# Revit family: BOLA DISC FLUSH
name_source: partatom
category: Lighting Fixtures
revit_build: Autodesk Revit 2017 (Build: 20160225_1515(x64)
units: mm (PartAtom-declared; Revit-internal decimal feet)

## family parameters
Always vertical = Yes
Cut with Voids When Loaded = No
Light Source = Yes
OmniClass Number = 23.80.70.00
OmniClass Title = Lighting
Part Type = Normal
Room Calculation Point = No
Round Connector Dimension = Use Diameter
Shared = No
Work Plane-Based = No

## types (4) — shared parameters
Color Filter = 16777215
Color Rendition Index = 95 CRI
Color Temperature = 2700K - 1800K (Warm Dim)
Dimming Lamp Color Temperature Shift = <None>
Emit Shape Visible in Rendering = No
Emit from Circle Diameter = 2' - 0"
Lifespan = 50K hour lifespan
Luminaire Efficacy = 65 Lumens/Watt (average)
Luminosity = 290Lm
Note = 3000K CCT models and 2700 CCT models
Power Consumption = 6W
Tilt Angle = 90.00°
Voltage = 120-277V 50/60Hz

## per-type parameters (varying)
| type | Photometric Web File |
| BOLA DISC FLUSH - 12 | bola4_IESNA2002_2018.ies |
| BOLA DISC FLUSH - 18 | bola5_IESNA2002_2018.ies |
| BOLA DISC FLUSH - 22 | bola6_IESNA2002_2018.ies |
| BOLA DISC FLUSH - 32 | bola8_IESNA2002_2018.ies |

type visibility flags: 4 boolean params named "<type name>" — each type sets only its own to Yes (folded from table)

## geometry (parser evidence)
native form markers: Sweep x2
no freeform markers — native parametric forms only
